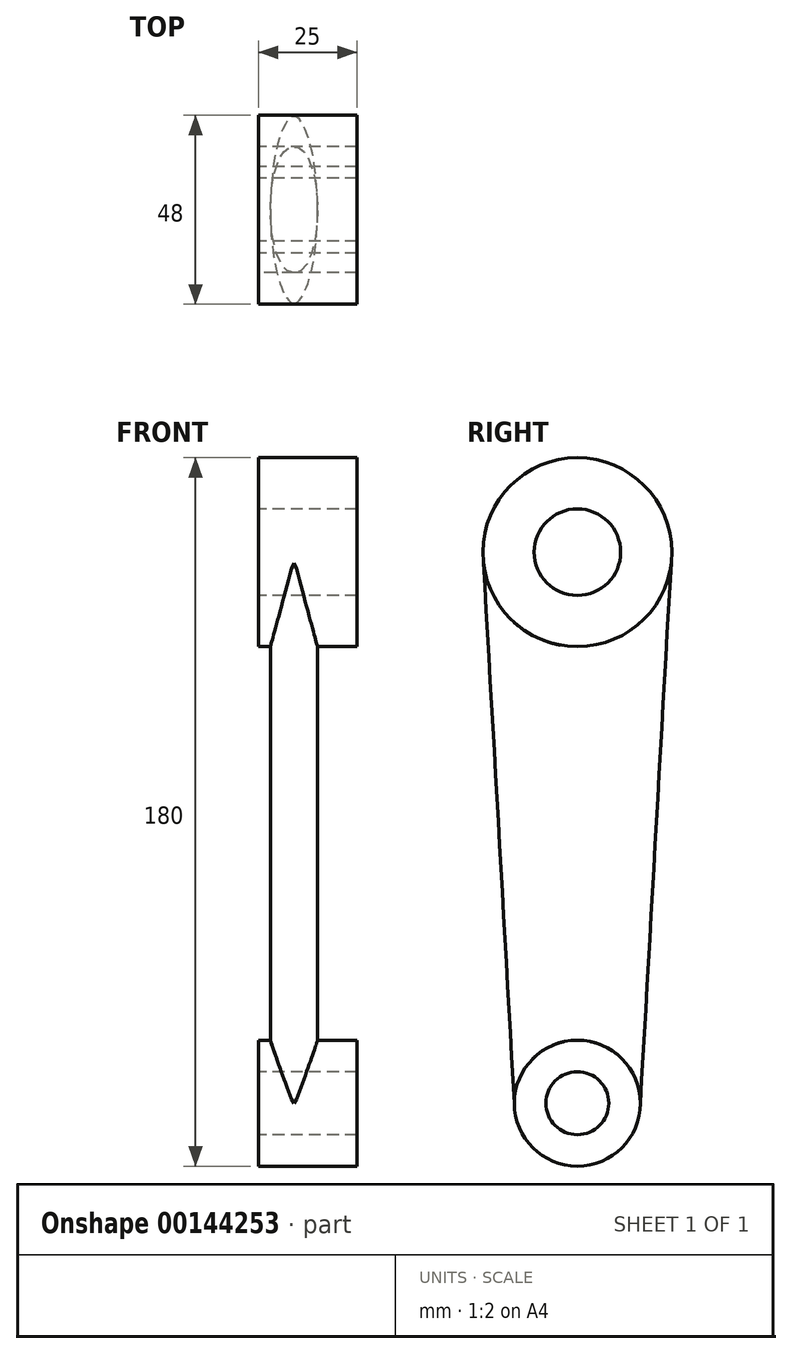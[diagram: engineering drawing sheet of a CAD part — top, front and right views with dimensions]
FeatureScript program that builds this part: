
annotation { "Feature Type Name" : "Feature", "Feature Type Description" : "" }
export const myFeature = defineFeature(function(context is Context, id is Id, definition is map)
    precondition{}
    {
        {
            var Q0;
            Q0=qCreatedBy(makeId("Right.planeOp"),FACE);
            var sketch = newSketch(context, id + "F0", { "sketchPlane" : qUnion([Q0])});
            skCircle(sketch, "E0", {"center": v(0, 140) * mm, "radius": 24 * mm});
            skCircle(sketch, "E1", {"center": v(0, 140) * mm, "radius": 11 * mm});
            skCircle(sketch, "E2", {"center": v(0, 0) * mm, "radius": 8 * mm});
            skCircle(sketch, "E3", {"center": v(0, 0) * mm, "radius": 16 * mm});
            skLineSegment(sketch, "E4", {"start": v(0, 140) * mm, "end": v(0, 140) * mm});
            skSolve(sketch);
        }
        {
            var Q0;
            Q0=makeQuery(id+"F0.imprint","IMPRINT",FACE,{"disambiguationData":[TD([[makeQuery(id+"F0.imprint","IMPRINT",EDGE,{"derivedFrom":sQuery(id+"F0.wireOp",EDGE,"E2")}),1.0]])]});
            var Q1;
            Q1=makeQuery(id+"F0.imprint","IMPRINT",FACE,{"disambiguationData":[TD([[makeQuery(id+"F0.imprint","IMPRINT",EDGE,{"derivedFrom":sQuery(id+"F0.wireOp",EDGE,"E2")}),-1.0]])]});
            extrude(context, id + "F1", {"entities" : qUnion([Q0, Q1]), "depth" : 25 * mm});
        }
        {
            var Q0;
            Q0=makeQuery(id+"F0.imprint","IMPRINT",FACE,{"disambiguationData":[TD([[makeQuery(id+"F0.imprint","IMPRINT",EDGE,{"derivedFrom":sQuery(id+"F0.wireOp",EDGE,"E0")}),1.0]])]});
            var Q1;
            Q1=makeQuery(id+"F0.imprint","IMPRINT",FACE,{"disambiguationData":[TD([[makeQuery(id+"F0.imprint","IMPRINT",EDGE,{"derivedFrom":sQuery(id+"F0.wireOp",EDGE,"E1")}),1.0]])]});
            extrude(context, id + "F2", {"entities" : qUnion([Q0, Q1]), "depth" : 25 * mm});
        }
        {
            var Q0;
            Q0=qCreatedBy(makeId("Top.planeOp"),FACE);
            var sketch = newSketch(context, id + "F3", { "sketchPlane" : qUnion([Q0])});
            skEllipse(sketch, "E5", {"center": v(9, 0) * mm, "majorRadius": 16 * mm, "minorRadius": 6 * mm, "majorAxis": v(0, -1)});
            skLineSegment(sketch, "E6.0", {"start": v(0, 16) * mm, "end": v(0, -16) * mm});
            skPoint(sketch, "E7", {"position": v(3, 0) * mm});
            skLineSegment(sketch, "E8", {"start": v(0, 16) * mm, "end": v(25, 16) * mm});
            skLineSegment(sketch, "E9", {"start": v(25, -16) * mm, "end": v(0, -16) * mm});
            skSolve(sketch);
        }
        {
            var Q0;
            Q0=sQuery(id+"F0.wireOp",VERTEX,"E0.center");
            var Q1;
            Q1=qCreatedBy(makeId("Top.planeOp"),FACE);
            cPlane(context, id + "F4", {"entities" : qUnion([Q0, Q1]), "cplaneType" : CPlaneType.PLANE_POINT, "offset" : 25 * mm, "width" : 150 * mm, "height" : 150 * mm});
        }
        {
            var Q0;
            Q0=qCreatedBy(id+"F4.planeOp",FACE);
            var sketch = newSketch(context, id + "F5", { "sketchPlane" : qUnion([Q0])});
            skEllipse(sketch, "E10.0", {"center": v(9, 0) * mm, "majorRadius": 24 * mm, "minorRadius": 6 * mm, "majorAxis": v(0, -1)});
            skLineSegment(sketch, "E11", {"start": v(0, 24) * mm, "end": v(25, 24) * mm});
            skLineSegment(sketch, "E12", {"start": v(25, -24) * mm, "end": v(0, -24) * mm});
            skSolve(sketch);
        }
        {
            var Q0;
            Q0=makeQuery(id+"F5.imprint","IMPRINT",FACE,{"disambiguationData":[TD([[makeQuery(id+"F5.imprint","IMPRINT",EDGE,{"derivedFrom":sQuery(id+"F5.wireOp",EDGE,"E10.0")}),1.0]])]});
            var Q1;
            {var subQ0=sQuery(id+"F3.wireOp",EDGE,"E5");var subQ1=makeQuery(id+"F3.imprint","INTERSECT",VERTEX,{"derivedFrom":[subQ0,sQuery(id+"F3.wireOp",EDGE,"E8")]});Q1=makeQuery(id+"F3.imprint","IMPRINT",FACE,{"disambiguationData":[TD([[makeQuery(id+"F3.imprint","IMPRINT",EDGE,{"disambiguationData":[TD([[subQ1,1.0]])],"derivedFrom":subQ0}),1.0]])]});}
            loft(context, id + "F6", {"operationType" : NewBodyOperationType.ADD, "sheetProfilesArray" : [{ "sheetProfileEntities" : qUnion([Q0]) }, { "sheetProfileEntities" : qUnion([Q1]) }]});
        }
        {
            var Q0;
            Q0=makeQuery(id+"F0.imprint","IMPRINT",FACE,{"disambiguationData":[TD([[makeQuery(id+"F0.imprint","IMPRINT",EDGE,{"derivedFrom":sQuery(id+"F0.wireOp",EDGE,"E1")}),1.0]])]});
            var Q1;
            Q1=makeQuery(id+"F0.imprint","IMPRINT",FACE,{"disambiguationData":[TD([[makeQuery(id+"F0.imprint","IMPRINT",EDGE,{"derivedFrom":sQuery(id+"F0.wireOp",EDGE,"E2")}),1.0]])]});
            extrude(context, id + "F7", {"entities" : qUnion([Q0, Q1]), "operationType" : NewBodyOperationType.REMOVE, "depth" : 25 * mm});
        }
    });
